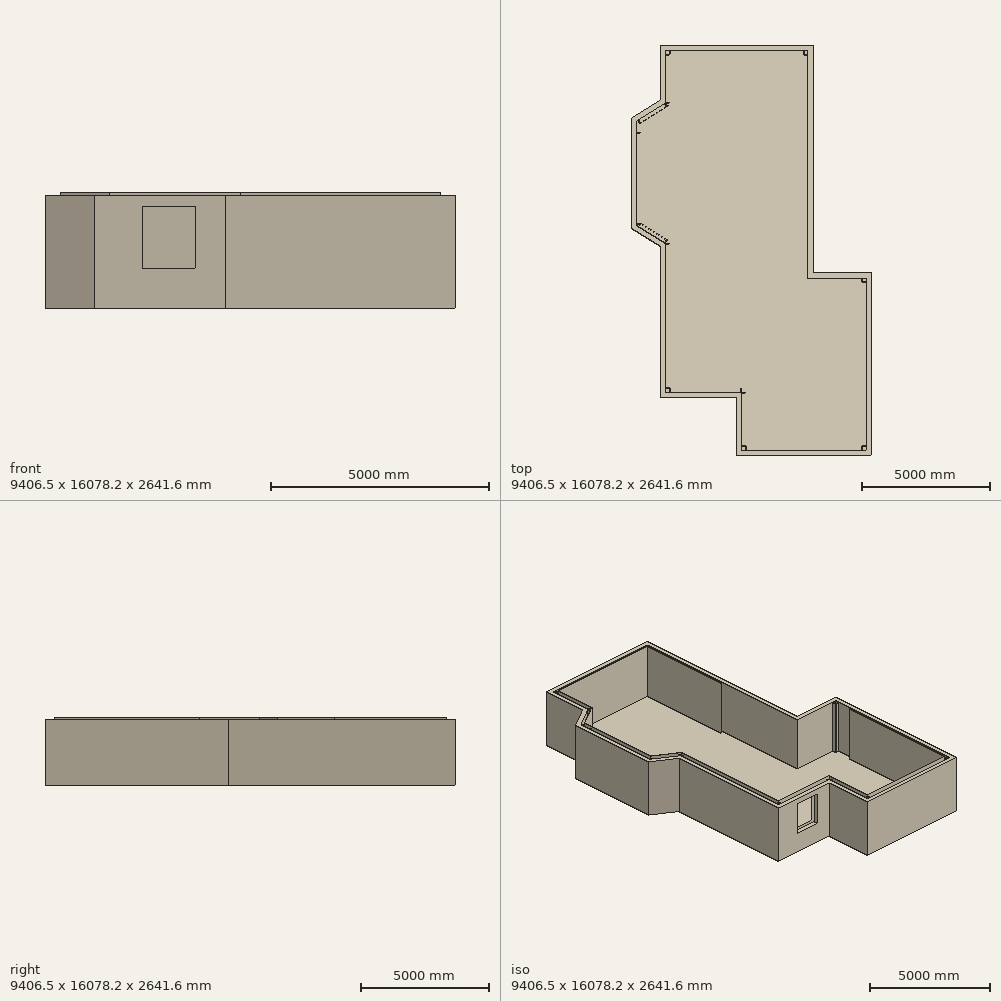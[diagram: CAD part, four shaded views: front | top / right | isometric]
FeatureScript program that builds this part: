
annotation { "Feature Type Name" : "Feature", "Feature Type Description" : "" }
export const myFeature = defineFeature(function(context is Context, id is Id, definition is map)
    precondition{}
    {
        {
            var Q0;
            Q0=qCreatedBy(makeId("Top.planeOp"),FACE);
            var sketch = newSketch(context, id + "F0", { "sketchPlane" : qUnion([Q0])});
            skLineSegment(sketch, "E0", {"start": v(-8280.4, 16078.2) * mm, "end": v(-2286, 16078.2) * mm});
            skLineSegment(sketch, "E1", {"start": v(-2286, 16078.2) * mm, "end": v(-2286, 7162.8) * mm});
            skLineSegment(sketch, "E2", {"start": v(-2286, 7162.8) * mm, "end": v(0, 7162.8) * mm});
            skLineSegment(sketch, "E3", {"start": v(0, 7162.8) * mm, "end": v(0, 0) * mm});
            skLineSegment(sketch, "E4", {"start": v(0, 0) * mm, "end": v(-5283.2, 0) * mm});
            skLineSegment(sketch, "E5", {"start": v(-5283.2, 0) * mm, "end": v(-5283.2, 2286) * mm});
            skLineSegment(sketch, "E6", {"start": v(-5283.2, 2286) * mm, "end": v(-8280.4, 2286) * mm});
            skLineSegment(sketch, "E7", {"start": v(-8280.4, 2286) * mm, "end": v(-8280.4, 8201.03) * mm});
            skLineSegment(sketch, "E8", {"start": v(-8280.4, 8201.03) * mm, "end": v(-9406.5, 8900.32) * mm});
            skLineSegment(sketch, "E9", {"start": v(-9406.5, 8900.32) * mm, "end": v(-9406.5, 13223.08) * mm});
            skLineSegment(sketch, "E10", {"start": v(-9406.5, 13223.08) * mm, "end": v(-8280.4, 13922.38) * mm});
            skLineSegment(sketch, "E11", {"start": v(-8280.4, 13922.38) * mm, "end": v(-8280.4, 16078.2) * mm});
            skSolve(sketch);
        }
        {
            var Q0;
            Q0=qSketchRegion(id+"F0",true);
            extrude(context, id + "F1", {"entities" : qUnion([Q0]), "depth" : 2578.1 * mm});
        }
        {
            var Q0;
            Q0=makeQuery(id+"F1.opExtrude","CAP_FACE",FACE,{"disambiguationData":[OSD([sQuery(id+"F0.wireOp",EDGE,"E0"),sQuery(id+"F0.wireOp",EDGE,"E1"),sQuery(id+"F0.wireOp",EDGE,"E2"),sQuery(id+"F0.wireOp",EDGE,"E3"),sQuery(id+"F0.wireOp",EDGE,"E4"),sQuery(id+"F0.wireOp",EDGE,"E5"),sQuery(id+"F0.wireOp",EDGE,"E6"),sQuery(id+"F0.wireOp",EDGE,"E7"),sQuery(id+"F0.wireOp",EDGE,"E8"),sQuery(id+"F0.wireOp",EDGE,"E9"),sQuery(id+"F0.wireOp",EDGE,"E10"),sQuery(id+"F0.wireOp",EDGE,"E11")])],"isStart":false});
            shell(context, id + "F2", {"entities" : qUnion([Q0]), "thickness" : 203.2 * mm});
        }
        {
            var Q0;
            Q0=makeQuery(id+"F2.opShell","OFFSET_FACE",FACE,{"disambiguationData":[OSD([sQuery(id+"F0.wireOp",EDGE,"E6")])]});
            var sketch = newSketch(context, id + "F3", { "sketchPlane" : qUnion([Q0])});
            skLineSegment(sketch, "E12.bottom", {"start": v(5969, 2324.1) * mm, "end": v(7188.2, 2324.1) * mm});
            skLineSegment(sketch, "E12.top", {"start": v(5969, 901.7) * mm, "end": v(7188.2, 901.7) * mm});
            skLineSegment(sketch, "E12.left", {"start": v(5969, 2324.1) * mm, "end": v(5969, 901.7) * mm});
            skLineSegment(sketch, "E12.right", {"start": v(7188.2, 2324.1) * mm, "end": v(7188.2, 901.7) * mm});
            skPoint(sketch, "E13", {"position": v(6578.6, 2324.1) * mm});
            skSolve(sketch);
        }
        {
            var Q0;
            Q0=makeQuery(id+"F2.opShell","OFFSET_FACE",FACE,{"disambiguationData":[OSD([sQuery(id+"F0.wireOp",EDGE,"E0"),sQuery(id+"F0.wireOp",EDGE,"E1"),sQuery(id+"F0.wireOp",EDGE,"E2"),sQuery(id+"F0.wireOp",EDGE,"E3"),sQuery(id+"F0.wireOp",EDGE,"E4"),sQuery(id+"F0.wireOp",EDGE,"E5"),sQuery(id+"F0.wireOp",EDGE,"E6"),sQuery(id+"F0.wireOp",EDGE,"E7"),sQuery(id+"F0.wireOp",EDGE,"E8"),sQuery(id+"F0.wireOp",EDGE,"E9"),sQuery(id+"F0.wireOp",EDGE,"E10"),sQuery(id+"F0.wireOp",EDGE,"E11")])]});
            var sketch = newSketch(context, id + "F4", { "sketchPlane" : qUnion([Q0])});
            skLineSegment(sketch, "E14.bottom", {"start": v(-8077.2, 13811.9) * mm, "end": v(-7937.5, 13811.9) * mm});
            skLineSegment(sketch, "E14.top", {"start": v(-8077.2, 13850) * mm, "end": v(-7937.5, 13850) * mm});
            skLineSegment(sketch, "E14.left", {"start": v(-8077.2, 13811.9) * mm, "end": v(-8077.2, 13850) * mm});
            skLineSegment(sketch, "E14.right", {"start": v(-7937.5, 13811.9) * mm, "end": v(-7937.5, 13850) * mm});
            skLineSegment(sketch, "E15.bottom", {"start": v(-7934.96, 15875) * mm, "end": v(-7896.86, 15875) * mm});
            skLineSegment(sketch, "E15.top", {"start": v(-7934.96, 15735.3) * mm, "end": v(-7896.86, 15735.3) * mm});
            skLineSegment(sketch, "E15.left", {"start": v(-7934.96, 15875) * mm, "end": v(-7934.96, 15735.3) * mm});
            skLineSegment(sketch, "E15.right", {"start": v(-7896.86, 15875) * mm, "end": v(-7896.86, 15735.3) * mm});
            skLineSegment(sketch, "E16.bottom", {"start": v(-8077.2, 15694.66) * mm, "end": v(-7937.5, 15694.66) * mm});
            skLineSegment(sketch, "E16.top", {"start": v(-8077.2, 15732.76) * mm, "end": v(-7937.5, 15732.76) * mm});
            skLineSegment(sketch, "E16.left", {"start": v(-8077.2, 15694.66) * mm, "end": v(-8077.2, 15732.76) * mm});
            skLineSegment(sketch, "E16.right", {"start": v(-7937.5, 15694.66) * mm, "end": v(-7937.5, 15732.76) * mm});
            skLineSegment(sketch, "E17.bottom", {"start": v(-2631.44, 15875) * mm, "end": v(-2669.54, 15875) * mm});
            skLineSegment(sketch, "E17.top", {"start": v(-2631.44, 15735.3) * mm, "end": v(-2669.54, 15735.3) * mm});
            skLineSegment(sketch, "E17.left", {"start": v(-2631.44, 15875) * mm, "end": v(-2631.44, 15735.3) * mm});
            skLineSegment(sketch, "E17.right", {"start": v(-2669.54, 15875) * mm, "end": v(-2669.54, 15735.3) * mm});
            skLineSegment(sketch, "E18.bottom", {"start": v(-2489.2, 15694.66) * mm, "end": v(-2628.9, 15694.66) * mm});
            skLineSegment(sketch, "E18.top", {"start": v(-2489.2, 15732.76) * mm, "end": v(-2628.9, 15732.76) * mm});
            skLineSegment(sketch, "E18.left", {"start": v(-2489.2, 15694.66) * mm, "end": v(-2489.2, 15732.76) * mm});
            skLineSegment(sketch, "E18.right", {"start": v(-2628.9, 15694.66) * mm, "end": v(-2628.9, 15732.76) * mm});
            skLineSegment(sketch, "E19", {"start": v(-8078.22, 13808.73) * mm, "end": v(-8110.59, 13788.64) * mm});
            skLineSegment(sketch, "E20", {"start": v(-8110.59, 13788.64) * mm, "end": v(-8036.89, 13669.96) * mm});
            skLineSegment(sketch, "E21", {"start": v(-8036.89, 13669.96) * mm, "end": v(-8004.52, 13690.06) * mm});
            skLineSegment(sketch, "E22", {"start": v(-8004.52, 13690.06) * mm, "end": v(-8078.22, 13808.73) * mm});
            skLineSegment(sketch, "E23.bottom", {"start": v(-9203.3, 12669.47) * mm, "end": v(-9063.6, 12669.47) * mm});
            skLineSegment(sketch, "E23.top", {"start": v(-9203.3, 12631.37) * mm, "end": v(-9063.6, 12631.37) * mm});
            skLineSegment(sketch, "E23.left", {"start": v(-9203.3, 12669.47) * mm, "end": v(-9203.3, 12631.37) * mm});
            skLineSegment(sketch, "E23.right", {"start": v(-9063.6, 12669.47) * mm, "end": v(-9063.6, 12631.37) * mm});
            skLineSegment(sketch, "E24", {"start": v(-9162.3, 13135.53) * mm, "end": v(-9129.94, 13155.63) * mm});
            skLineSegment(sketch, "E25", {"start": v(-9129.94, 13155.63) * mm, "end": v(-9056.24, 13036.95) * mm});
            skLineSegment(sketch, "E26", {"start": v(-9056.24, 13036.95) * mm, "end": v(-9088.6, 13016.85) * mm});
            skLineSegment(sketch, "E27", {"start": v(-9088.6, 13016.85) * mm, "end": v(-9162.3, 13135.53) * mm});
            skLineSegment(sketch, "E28", {"start": v(-9162.3, 8987.87) * mm, "end": v(-9088.6, 9106.55) * mm});
            skLineSegment(sketch, "E29", {"start": v(-9088.6, 9106.55) * mm, "end": v(-9056.24, 9086.45) * mm});
            skLineSegment(sketch, "E30", {"start": v(-9056.24, 9086.45) * mm, "end": v(-9129.94, 8967.77) * mm});
            skLineSegment(sketch, "E31", {"start": v(-9129.94, 8967.77) * mm, "end": v(-9162.3, 8987.87) * mm});
            skLineSegment(sketch, "E32", {"start": v(-8109.57, 8334.13) * mm, "end": v(-8077.2, 8314.03) * mm});
            skLineSegment(sketch, "E33", {"start": v(-8077.2, 8314.03) * mm, "end": v(-8003.5, 8432.71) * mm});
            skLineSegment(sketch, "E34", {"start": v(-8003.5, 8432.71) * mm, "end": v(-8035.87, 8452.81) * mm});
            skLineSegment(sketch, "E35", {"start": v(-8035.87, 8452.81) * mm, "end": v(-8109.57, 8334.13) * mm});
            skLineSegment(sketch, "E36.bottom", {"start": v(-9203.3, 9061.59) * mm, "end": v(-9063.6, 9061.59) * mm});
            skLineSegment(sketch, "E36.top", {"start": v(-9203.3, 9099.69) * mm, "end": v(-9063.6, 9099.69) * mm});
            skLineSegment(sketch, "E36.left", {"start": v(-9203.3, 9061.59) * mm, "end": v(-9203.3, 9099.69) * mm});
            skLineSegment(sketch, "E36.right", {"start": v(-9063.6, 9061.59) * mm, "end": v(-9063.6, 9099.69) * mm});
            skLineSegment(sketch, "E37.bottom", {"start": v(-8077.2, 8311.5) * mm, "end": v(-7937.5, 8311.5) * mm});
            skLineSegment(sketch, "E37.top", {"start": v(-8077.2, 8273.4) * mm, "end": v(-7937.5, 8273.4) * mm});
            skLineSegment(sketch, "E37.left", {"start": v(-8077.2, 8311.5) * mm, "end": v(-8077.2, 8273.4) * mm});
            skLineSegment(sketch, "E37.right", {"start": v(-7937.5, 8311.5) * mm, "end": v(-7937.5, 8273.4) * mm});
            skLineSegment(sketch, "E38.bottom", {"start": v(-8077.2, 2631.44) * mm, "end": v(-7937.5, 2631.44) * mm});
            skLineSegment(sketch, "E38.top", {"start": v(-8077.2, 2669.54) * mm, "end": v(-7937.5, 2669.54) * mm});
            skLineSegment(sketch, "E38.left", {"start": v(-8077.2, 2631.44) * mm, "end": v(-8077.2, 2669.54) * mm});
            skLineSegment(sketch, "E38.right", {"start": v(-7937.5, 2631.44) * mm, "end": v(-7937.5, 2669.54) * mm});
            skLineSegment(sketch, "E39.bottom", {"start": v(-7896.86, 2489.2) * mm, "end": v(-7934.96, 2489.2) * mm});
            skLineSegment(sketch, "E39.top", {"start": v(-7896.86, 2628.9) * mm, "end": v(-7934.96, 2628.9) * mm});
            skLineSegment(sketch, "E39.left", {"start": v(-7896.86, 2489.2) * mm, "end": v(-7896.86, 2628.9) * mm});
            skLineSegment(sketch, "E39.right", {"start": v(-7934.96, 2489.2) * mm, "end": v(-7934.96, 2628.9) * mm});
            skLineSegment(sketch, "E40.bottom", {"start": v(-5082.54, 2489.2) * mm, "end": v(-5120.64, 2489.2) * mm});
            skLineSegment(sketch, "E40.top", {"start": v(-5082.54, 2628.9) * mm, "end": v(-5120.64, 2628.9) * mm});
            skLineSegment(sketch, "E40.left", {"start": v(-5082.54, 2489.2) * mm, "end": v(-5082.54, 2628.9) * mm});
            skLineSegment(sketch, "E40.right", {"start": v(-5120.64, 2489.2) * mm, "end": v(-5120.64, 2628.9) * mm});
            skLineSegment(sketch, "E41.top", {"start": v(-5080, 2448.56) * mm, "end": v(-4940.3, 2448.56) * mm});
            skLineSegment(sketch, "E41.right", {"start": v(-4940.3, 2486.66) * mm, "end": v(-4940.3, 2448.56) * mm});
            skLineSegment(sketch, "E42.bottom", {"start": v(-5080, 345.44) * mm, "end": v(-4940.3, 345.44) * mm});
            skLineSegment(sketch, "E42.top", {"start": v(-5080, 383.54) * mm, "end": v(-4940.3, 383.54) * mm});
            skLineSegment(sketch, "E42.left", {"start": v(-5080, 345.44) * mm, "end": v(-5080, 383.54) * mm});
            skLineSegment(sketch, "E42.right", {"start": v(-4940.3, 345.44) * mm, "end": v(-4940.3, 383.54) * mm});
            skLineSegment(sketch, "E43.bottom", {"start": v(-4937.76, 203.2) * mm, "end": v(-4899.66, 203.2) * mm});
            skLineSegment(sketch, "E43.top", {"start": v(-4937.76, 342.9) * mm, "end": v(-4899.66, 342.9) * mm});
            skLineSegment(sketch, "E43.left", {"start": v(-4937.76, 203.2) * mm, "end": v(-4937.76, 342.9) * mm});
            skLineSegment(sketch, "E43.right", {"start": v(-4899.66, 203.2) * mm, "end": v(-4899.66, 342.9) * mm});
            skLineSegment(sketch, "E44.bottom", {"start": v(-383.54, 203.2) * mm, "end": v(-345.44, 203.2) * mm});
            skLineSegment(sketch, "E44.top", {"start": v(-383.54, 342.9) * mm, "end": v(-345.44, 342.9) * mm});
            skLineSegment(sketch, "E44.left", {"start": v(-383.54, 203.2) * mm, "end": v(-383.54, 342.9) * mm});
            skLineSegment(sketch, "E44.right", {"start": v(-345.44, 203.2) * mm, "end": v(-345.44, 342.9) * mm});
            skLineSegment(sketch, "E45.bottom", {"start": v(-203.2, 345.44) * mm, "end": v(-342.9, 345.44) * mm});
            skLineSegment(sketch, "E45.top", {"start": v(-203.2, 383.54) * mm, "end": v(-342.9, 383.54) * mm});
            skLineSegment(sketch, "E45.left", {"start": v(-203.2, 345.44) * mm, "end": v(-203.2, 383.54) * mm});
            skLineSegment(sketch, "E45.right", {"start": v(-342.9, 345.44) * mm, "end": v(-342.9, 383.54) * mm});
            skLineSegment(sketch, "E46.bottom", {"start": v(-203.2, 6779.26) * mm, "end": v(-342.9, 6779.26) * mm});
            skLineSegment(sketch, "E46.top", {"start": v(-203.2, 6817.36) * mm, "end": v(-342.9, 6817.36) * mm});
            skLineSegment(sketch, "E46.left", {"start": v(-203.2, 6779.26) * mm, "end": v(-203.2, 6817.36) * mm});
            skLineSegment(sketch, "E46.right", {"start": v(-342.9, 6779.26) * mm, "end": v(-342.9, 6817.36) * mm});
            skLineSegment(sketch, "E47.bottom", {"start": v(-345.44, 6959.6) * mm, "end": v(-383.54, 6959.6) * mm});
            skLineSegment(sketch, "E47.top", {"start": v(-345.44, 6819.9) * mm, "end": v(-383.54, 6819.9) * mm});
            skLineSegment(sketch, "E47.left", {"start": v(-345.44, 6959.6) * mm, "end": v(-345.44, 6819.9) * mm});
            skLineSegment(sketch, "E47.right", {"start": v(-383.54, 6959.6) * mm, "end": v(-383.54, 6819.9) * mm});
            skLineSegment(sketch, "E48", {"start": v(-4940.3, 2486.66) * mm, "end": v(-5080, 2486.66) * mm});
            skLineSegment(sketch, "E49", {"start": v(-5080, 2486.66) * mm, "end": v(-5080, 2448.56) * mm});
            skLineSegment(sketch, "E50", {"start": v(-9203.3, 13110.07) * mm, "end": v(-9045.7, 12987.43) * mm, "construction": true});
            skLineSegment(sketch, "E51", {"start": v(-9045.7, 12987.43) * mm, "end": v(-9104.83, 13171.22) * mm, "construction": true});
            skLineSegment(sketch, "E52", {"start": v(-9104.83, 13171.22) * mm, "end": v(-9203.3, 12968.55) * mm, "construction": true});
            skLineSegment(sketch, "E53", {"start": v(-9203.3, 12968.55) * mm, "end": v(-9045.7, 12987.43) * mm, "construction": true});
            skSolve(sketch);
        }
        {
            var Q0;
            Q0=qSketchRegion(id+"F3",true);
            var Q1;
            Q1=makeQuery(id+"FwcOo8eikqoZCvb_1.opExtrude","SWEPT_FACE",FACE,{"disambiguationData":[OSD([sQuery(id+"F7.wireOp",EDGE,"E55.top"),sQuery(id+"F7.wireOp",EDGE,"E63")])]});
            extrude(context, id + "F5", {"entities" : qUnion([Q0]), "operationType" : NewBodyOperationType.REMOVE, "endBound" : BoundingType.UP_TO_NEXT, "oppositeDirection" : true, "depth" : 25.4 * mm});
        }
        {
            var Q0;
            Q0=qSketchRegion(id+"F4",true);
            extrude(context, id + "F6", {"entities" : qUnion([Q0]), "operationType" : NewBodyOperationType.ADD, "depth" : 2349.5 * mm});
        }
        {
            var Q0;
            Q0=makeQuery(id+"F2.opShell","OFFSET_FACE",FACE,{"disambiguationData":[OSD([sQuery(id+"F0.wireOp",EDGE,"E0"),sQuery(id+"F0.wireOp",EDGE,"E1"),sQuery(id+"F0.wireOp",EDGE,"E2"),sQuery(id+"F0.wireOp",EDGE,"E3"),sQuery(id+"F0.wireOp",EDGE,"E4"),sQuery(id+"F0.wireOp",EDGE,"E5"),sQuery(id+"F0.wireOp",EDGE,"E6"),sQuery(id+"F0.wireOp",EDGE,"E7"),sQuery(id+"F0.wireOp",EDGE,"E8"),sQuery(id+"F0.wireOp",EDGE,"E9"),sQuery(id+"F0.wireOp",EDGE,"E10"),sQuery(id+"F0.wireOp",EDGE,"E11")])]});
            var sketch = newSketch(context, id + "F7", { "sketchPlane" : qUnion([Q0])});
            skLineSegment(sketch, "E54.bottom", {"start": v(-7937.5, 8391.73) * mm, "end": v(-7924.8, 8391.73) * mm, "construction": true});
            skLineSegment(sketch, "E54.top", {"start": v(-7937.5, 2641.6) * mm, "end": v(-7924.8, 2641.6) * mm, "construction": true});
            skLineSegment(sketch, "E54.left", {"start": v(-7937.5, 8391.73) * mm, "end": v(-7937.5, 2641.6) * mm});
            skLineSegment(sketch, "E54.right", {"start": v(-7924.8, 8391.73) * mm, "end": v(-7924.8, 2641.6) * mm});
            skLineSegment(sketch, "E55.bottom", {"start": v(-7924.8, 2628.9) * mm, "end": v(-4940.3, 2628.9) * mm});
            skLineSegment(sketch, "E55.top", {"start": v(-7924.8, 2641.6) * mm, "end": v(-4940.3, 2641.6) * mm});
            skLineSegment(sketch, "E55.left", {"start": v(-7924.8, 2628.9) * mm, "end": v(-7924.8, 2641.6) * mm, "construction": true});
            skLineSegment(sketch, "E55.right", {"start": v(-4940.3, 2628.9) * mm, "end": v(-4940.3, 2641.6) * mm, "construction": true});
            skLineSegment(sketch, "E56", {"start": v(-7924.8, 2628.9) * mm, "end": v(-7937.5, 2628.9) * mm});
            skLineSegment(sketch, "E57", {"start": v(-7937.5, 2628.9) * mm, "end": v(-7937.5, 2641.6) * mm});
            skLineSegment(sketch, "E58.bottom", {"start": v(-4940.3, 2628.9) * mm, "end": v(-4927.6, 2628.9) * mm, "construction": true});
            skLineSegment(sketch, "E58.top", {"start": v(-4940.3, 355.6) * mm, "end": v(-4927.6, 355.6) * mm, "construction": true});
            skLineSegment(sketch, "E58.left", {"start": v(-4940.3, 2628.9) * mm, "end": v(-4940.3, 355.6) * mm});
            skLineSegment(sketch, "E58.right", {"start": v(-4927.6, 2628.9) * mm, "end": v(-4927.6, 355.6) * mm});
            skLineSegment(sketch, "E59.bottom", {"start": v(-4927.6, 342.9) * mm, "end": v(-355.6, 342.9) * mm});
            skLineSegment(sketch, "E59.top", {"start": v(-4927.6, 355.6) * mm, "end": v(-355.6, 355.6) * mm});
            skLineSegment(sketch, "E59.left", {"start": v(-4927.6, 342.9) * mm, "end": v(-4927.6, 355.6) * mm, "construction": true});
            skLineSegment(sketch, "E59.right", {"start": v(-355.6, 342.9) * mm, "end": v(-355.6, 355.6) * mm, "construction": true});
            skLineSegment(sketch, "E60", {"start": v(-4940.3, 355.6) * mm, "end": v(-4940.3, 342.9) * mm});
            skLineSegment(sketch, "E61", {"start": v(-4940.3, 342.9) * mm, "end": v(-4927.6, 342.9) * mm});
            skLineSegment(sketch, "E62", {"start": v(-4927.6, 2628.9) * mm, "end": v(-4927.6, 2641.6) * mm});
            skLineSegment(sketch, "E63", {"start": v(-4940.3, 2641.6) * mm, "end": v(-4927.6, 2641.6) * mm});
            skLineSegment(sketch, "E64.bottom", {"start": v(-355.6, 355.6) * mm, "end": v(-342.9, 355.6) * mm, "construction": true});
            skLineSegment(sketch, "E64.top", {"start": v(-355.6, 6019.58) * mm, "end": v(-342.9, 6019.58) * mm});
            skLineSegment(sketch, "E64.left", {"start": v(-355.6, 355.6) * mm, "end": v(-355.6, 6019.58) * mm});
            skLineSegment(sketch, "E64.right", {"start": v(-342.9, 355.6) * mm, "end": v(-342.9, 6019.58) * mm});
            skLineSegment(sketch, "E65", {"start": v(-355.6, 342.9) * mm, "end": v(-342.9, 342.9) * mm});
            skLineSegment(sketch, "E66", {"start": v(-342.9, 342.9) * mm, "end": v(-342.9, 355.6) * mm});
            skLineSegment(sketch, "E67", {"start": v(-7937.5, 8391.73) * mm, "end": v(-9063.6, 9091.02) * mm});
            skLineSegment(sketch, "E68", {"start": v(-9063.6, 9091.02) * mm, "end": v(-9063.6, 13032.38) * mm});
            skLineSegment(sketch, "E69", {"start": v(-9063.6, 13032.38) * mm, "end": v(-7937.5, 13731.67) * mm});
            skLineSegment(sketch, "E70", {"start": v(-7937.5, 13731.67) * mm, "end": v(-7937.5, 15735.3) * mm});
            skLineSegment(sketch, "E71", {"start": v(-7937.5, 15735.3) * mm, "end": v(-2628.9, 15735.3) * mm});
            skLineSegment(sketch, "E72", {"start": v(-2628.9, 15735.3) * mm, "end": v(-2628.9, 11339.58) * mm});
            skLineSegment(sketch, "E73", {"start": v(-2628.9, 11339.58) * mm, "end": v(-2641.6, 11339.58) * mm});
            skLineSegment(sketch, "E74", {"start": v(-2641.6, 11339.58) * mm, "end": v(-2641.6, 15722.6) * mm});
            skLineSegment(sketch, "E75", {"start": v(-2641.6, 15722.6) * mm, "end": v(-7924.8, 15722.6) * mm});
            skLineSegment(sketch, "E76", {"start": v(-7924.8, 15722.6) * mm, "end": v(-7924.8, 13724.61) * mm});
            skLineSegment(sketch, "E77", {"start": v(-7924.8, 13724.61) * mm, "end": v(-9050.9, 13025.32) * mm});
            skLineSegment(sketch, "E78", {"start": v(-9050.9, 13025.32) * mm, "end": v(-9050.9, 9098.08) * mm});
            skLineSegment(sketch, "E79", {"start": v(-9050.9, 9098.08) * mm, "end": v(-7924.8, 8398.79) * mm});
            skLineSegment(sketch, "E80", {"start": v(-8493.85, 8752.16) * mm, "end": v(-8500.55, 8741.37) * mm, "construction": true});
            skLineSegment(sketch, "E81", {"start": v(-9063.6, 11061.7) * mm, "end": v(-9050.9, 11061.7) * mm, "construction": true});
            skLineSegment(sketch, "E82", {"start": v(-8487.85, 13374.97) * mm, "end": v(-8494.55, 13385.75) * mm, "construction": true});
            skLineSegment(sketch, "E83", {"start": v(-7924.8, 15722.6) * mm, "end": v(-7937.5, 15722.6) * mm, "construction": true});
            skLineSegment(sketch, "E84", {"start": v(-2641.6, 15735.3) * mm, "end": v(-2641.6, 15722.6) * mm, "construction": true});
            skLineSegment(sketch, "E85", {"start": v(-7924.8, 8391.73) * mm, "end": v(-7924.8, 8398.79) * mm});
            skSolve(sketch);
        }
        {
            var Q0;
            Q0 = qSketchRegion(id + "F7", true);
            extrude(context, id + "F8", {"entities" : qUnion([Q0]), "depth" : 12 * 203.2 * mm});
        }
        {
            var Q0;
            Q0 = qSketchRegion(id + "F3", true);
            var Q1;
            Q1=makeQuery(id+"F8.opExtrude","SWEPT_FACE",FACE,{"disambiguationData":[OSD([sQuery(id+"F7.wireOp",EDGE,"E55.top"),sQuery(id+"F7.wireOp",EDGE,"E63")])]});
            extrude(context, id + "F9", {"entities" : qUnion([Q0]), "operationType" : NewBodyOperationType.REMOVE, "endBound" : BoundingType.UP_TO_SURFACE, "endBoundEntityFace" : qUnion([Q1]), "depth" : 25.4 * mm});
        }
    });
